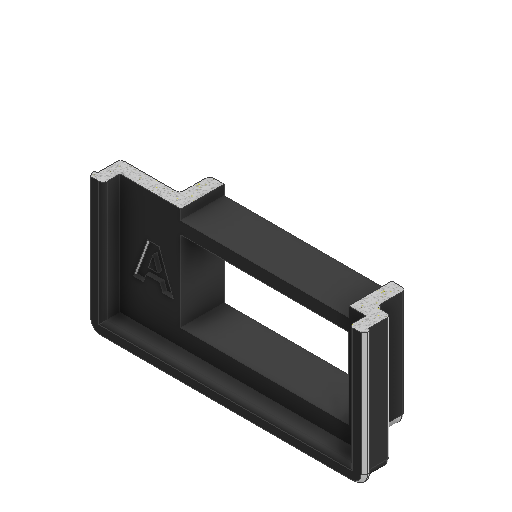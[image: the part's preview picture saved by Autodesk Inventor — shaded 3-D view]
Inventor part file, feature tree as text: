
AUTODESK INVENTOR PART (.ipt)
format: ipt  version: 2025 (Build 290162000, 162)  size: 364,032 bytes
history: native  units: mm
features: reference x51, sketch x9, extrude x6, other x6, fillet x2, emboss x1, sweep x1, projected_geometry x1
ambient origin geometry x8: Origin, YZ Plane, XZ Plane, XY Plane, X Axis, Y Axis, Z Axis, Center Point
bodies: Solid1 (feature_tree)
feature tree (77):
  extrude  "Extrusion1"  Depth=50.0mm
  extrude  "Extrusion2"  Depth=7.0mm TaperAngle=0.0deg
  extrude  "Extrusion3"  Depth=3.1mm
  extrude  "Extrusion4"  Depth=0.35mm
  extrude  "Extrusion5"  Depth=4.0mm TaperAngle=0.0deg
  extrude  "Extrusion6"  Depth=15.0mm
  emboss  "Emboss1"
  fillet  "Fillet3"  Radius=8.726646mm
  fillet  "Fillet2"  Radius=6.981317mm
  sweep  "Sweep3"
  sketch  "Sketch1"  dims[d0=60.0mm d1=50.0mm]
  sketch  "Sketch2"  dims[d2=7.0mm d3=0.0mm d6=7.0mm d7=0.0mm]
  sketch  "Sketch3"  dims[d8=3.1mm d9=0.0mm d10=3.0mm]
  reference  "Reference2"
  sketch  "Sketch4"  dims[d11=4.0mm d12=0.0mm d13=0.35mm]
  reference  "Reference3"
  reference  "Reference4"
  reference  "Reference5"
  reference  "Reference6"
  reference  "Reference7"
  reference  "Reference8"
  reference  "Reference9"
  reference  "Reference10"
  sketch  "Sketch5"  dims[d14=0.35mm d15=4.0mm d16=0.0mm]
  reference  "Reference11"
  reference  "Reference12"
  reference  "Reference13"
  reference  "Reference14"
  reference  "Reference15"
  reference  "Reference16"
  reference  "Reference17"
  reference  "Reference18"
  reference  "Reference21"
  reference  "Reference22"
  reference  "Reference23"
  reference  "Reference24"
  reference  "Reference25"
  reference  "Reference26"
  reference  "Reference27"
  reference  "Reference28"
  reference  "Reference29"
  reference  "Reference30"
  reference  "Reference31"
  reference  "Reference32"
  reference  "Reference33"
  reference  "Reference34"
  reference  "Reference35"
  reference  "Reference36"
  sketch  "Sketch11"  dims[d27=0.25mm d29=15.0mm d38=8.726646mm d39=6.981317mm]
  reference  "Reference37"
  sketch  "Sketch12"  dims[d40=0.3mm d43=0.75mm]
  reference  "Reference39"
  sketch  "Sketch13"  dims[d46=3.5mm d48=0.7mm d49=0.0mm d52=8.0mm d53=16.0mm d54=8.0mm d55=8.0mm d56=1.5mm d57=0.0mm d58=2.0mm d59=0.0mm d60=0.0mm d62=7.39429mm d64=1.4mm d65=7.3mm d66=3.5mm d67=7.026096mm d68=1.4mm]
  reference  "Reference40"
  reference  "Reference41"
  projected_geometry  "Projected Loop3"
  reference  "Reference42"
  reference  "Reference43"
  reference  "Reference44"
  reference  "Reference45"
  reference  "Reference46"
  reference  "Reference47"
  reference  "Reference48"
  reference  "Reference49"
  reference  "Reference50"
  reference  "Reference51"
  reference  "Reference52"
  reference  "Reference53"
  reference  "Reference54"
  reference  "Reference55"
  sketch  "3D Sketch3"
  other  "USB_C_PD_PPS_sink_with_enclosure.iam"
  other  "top_enclosure:1"
  other  "USB_C_PD_PPS_sink:1"
  other  "3461AS_3461AS-1:2"
  other  "3461AS_3461AS-1:1"
  other  "G800LW304032EU-Footprint-1_CMP-002-00028-3:1"
